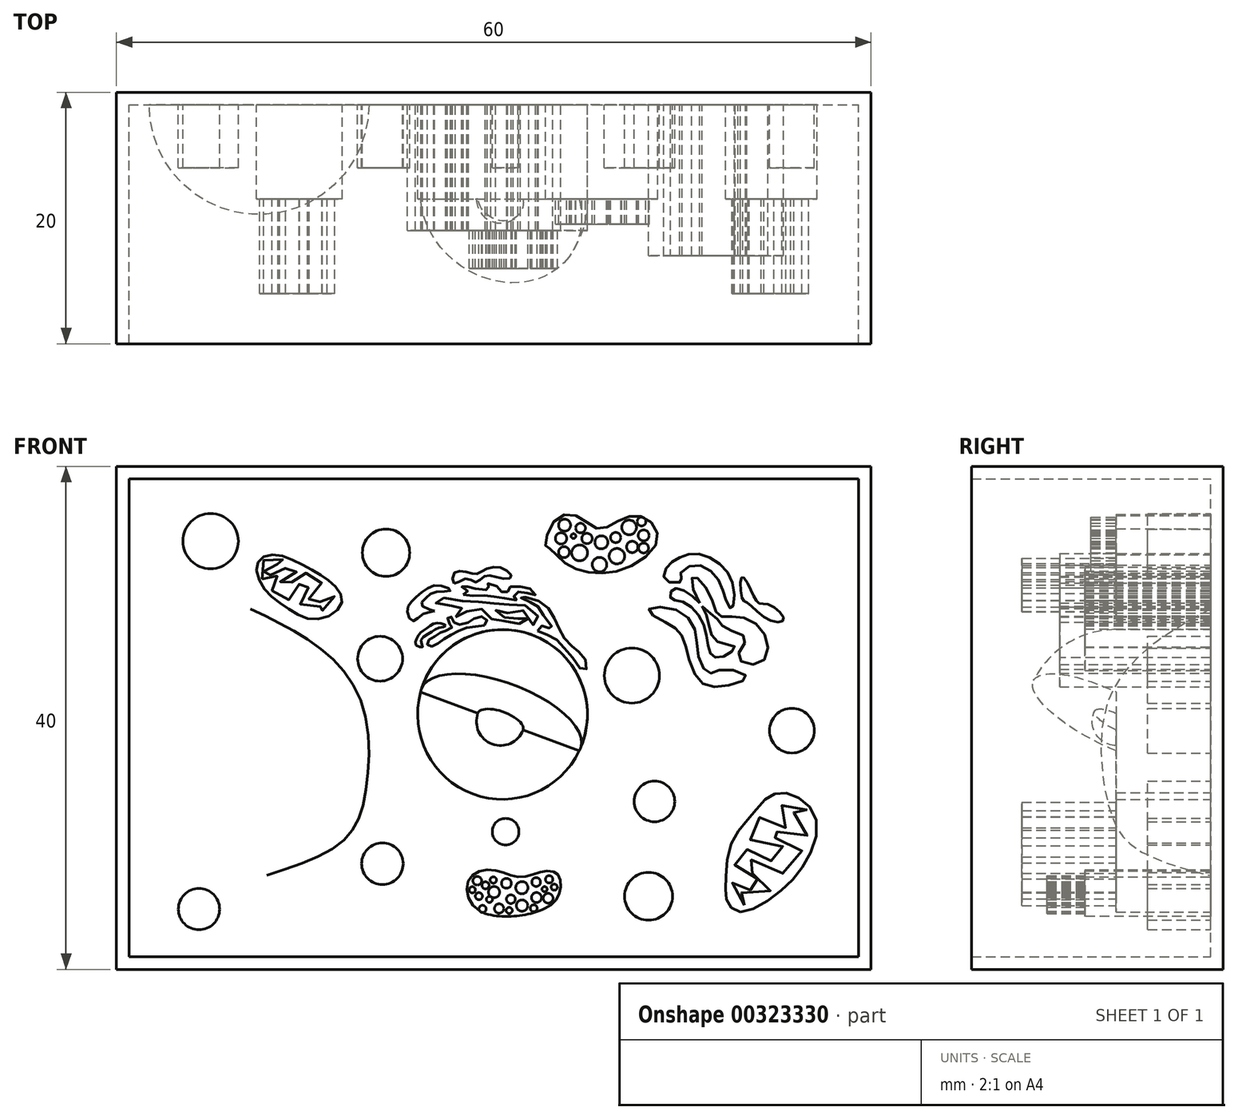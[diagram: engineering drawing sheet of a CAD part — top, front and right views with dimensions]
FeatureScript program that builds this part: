
annotation { "Feature Type Name" : "Feature", "Feature Type Description" : "" }
export const myFeature = defineFeature(function(context is Context, id is Id, definition is map)
    precondition{}
    {
        {
            var Q0;
            Q0=qCreatedBy(makeId("Front.planeOp"),FACE);
            var sketch = newSketch(context, id + "F0", { "sketchPlane" : qUnion([Q0])});
            skLineSegment(sketch, "E0.bottom", {"start": v(0, 0) * mm, "end": v(60, 0) * mm});
            skLineSegment(sketch, "E0.top", {"start": v(0, 40) * mm, "end": v(60, 40) * mm});
            skLineSegment(sketch, "E0.left", {"start": v(0, 0) * mm, "end": v(0, 40) * mm});
            skLineSegment(sketch, "E0.right", {"start": v(60, 0) * mm, "end": v(60, 40) * mm});
            skSolve(sketch);
        }
        {
            var Q0;
            Q0 = qSketchRegion(id + "F0", true);
            extrude(context, id + "F1", {"entities" : qUnion([Q0]), "depth" : 20 * mm});
        }
        {
            var Q0;
            Q0=makeQuery(id+"F1.opExtrude","CAP_FACE",FACE,{"disambiguationData":[OSD([sQuery(id+"F0.wireOp",EDGE,"E0.bottom"),sQuery(id+"F0.wireOp",EDGE,"E0.top"),sQuery(id+"F0.wireOp",EDGE,"E0.left"),sQuery(id+"F0.wireOp",EDGE,"E0.right")])],"isStart":false});
            shell(context, id + "F2", {"entities" : qUnion([Q0]), "thickness" : 1 * mm});
        }
        {
            var Q0;
            Q0=makeQuery(id+"F2.opShell","OFFSET_FACE",FACE,{"disambiguationData":[OSD([sQuery(id+"F0.wireOp",EDGE,"E0.bottom"),sQuery(id+"F0.wireOp",EDGE,"E0.top"),sQuery(id+"F0.wireOp",EDGE,"E0.left"),sQuery(id+"F0.wireOp",EDGE,"E0.right")])]});
            var sketch = newSketch(context, id + "F3", { "sketchPlane" : qUnion([Q0])});
            skCircle(sketch, "E1", {"center": v(30.7, 20.27) * mm, "radius": 6.75 * mm});
            skSolve(sketch);
        }
        {
            var Q0;
            Q0 = qSketchRegion(id + "F3", true);
            extrude(context, id + "F4", {"entities" : qUnion([Q0]), "operationType" : NewBodyOperationType.ADD, "depth" : 7.5 * mm});
        }
        {
            var Q0;
            Q0=makeQuery(id+"F4.opExtrude","CAP_FACE",FACE,{"disambiguationData":[OSD([sQuery(id+"F3.wireOp",EDGE,"E1")])],"isStart":false});
            var sketch = newSketch(context, id + "F5", { "sketchPlane" : qUnion([Q0])});
            skLineSegment(sketch, "E2", {"start": v(24.19, 22.06) * mm, "end": v(36.8, 17.38) * mm});
            skArc(sketch, "E3", {"start": v(36.8, 17.38) * mm, "mid": v(33.07, 26.67) * mm, "end": v(24.19, 22.06) * mm});
            skSolve(sketch);
        }
        {
            var Q0;
            {var subQ0=sQuery(id+"F5.wireOp",EDGE,"E2");Q0=makeQuery(id+"F5.imprint","IMPRINT",FACE,{"disambiguationData":[TD([[makeQuery(id+"F5.imprint","IMPRINT",EDGE,{"derivedFrom":subQ0}),1.0]])]});}
            var Q1;
            Q1=sQuery(id+"F5.wireOp",EDGE,"E2");
            revolve(context, id + "F6", {"operationType" : NewBodyOperationType.ADD, "entities" : qUnion([Q0]), "axis" : qUnion([Q1]), "revolveType" : RevolveType.ONE_DIRECTION, "angle" : 65 * degree});
        }
        {
            var Q0;
            Q0=makeQuery(id+"F4.opExtrude","CAP_FACE",FACE,{"disambiguationData":[OSD([sQuery(id+"F3.wireOp",EDGE,"E1")])],"isStart":false});
            var sketch = newSketch(context, id + "F7", { "sketchPlane" : qUnion([Q0])});
            skLineSegment(sketch, "E4", {"start": v(28.74, 20.37) * mm, "end": v(32.34, 19.04) * mm});
            skArc(sketch, "E5", {"start": v(28.74, 20.37) * mm, "mid": v(29.88, 17.92) * mm, "end": v(32.34, 19.04) * mm});
            skSolve(sketch);
        }
        {
            var Q0;
            Q0 = qSketchRegion(id + "F7", true);
            var Q1;
            Q1=sQuery(id+"F7.wireOp",EDGE,"E4");
            revolve(context, id + "F8", {"operationType" : NewBodyOperationType.ADD, "entities" : qUnion([Q0]), "axis" : qUnion([Q1]), "revolveType" : RevolveType.FULL});
        }
        {
            var Q0;
            Q0=makeQuery(id+"F2.opShell","OFFSET_FACE",FACE,{"disambiguationData":[OSD([sQuery(id+"F0.wireOp",EDGE,"E0.bottom"),sQuery(id+"F0.wireOp",EDGE,"E0.top"),sQuery(id+"F0.wireOp",EDGE,"E0.left"),sQuery(id+"F0.wireOp",EDGE,"E0.right")])]});
            var sketch = newSketch(context, id + "F9", { "sketchPlane" : qUnion([Q0])});
            skFitSpline(sketch, "E6", {"points": [v(25.07, 25.66) * mm, v(25.73, 26.04) * mm, v(26.42, 26.5) * mm, v(27.33, 26.99) * mm, v(28.44, 27.27) * mm, v(29.4, 27.44) * mm, v(29.35, 27.95) * mm, v(28.58, 27.98) * mm, v(27.9, 27.55) * mm, v(27, 27.46) * mm, v(26.76, 27.82) * mm, v(26.47, 28.12) * mm, v(26.35, 27.59) * mm, v(26.73, 27.3) * mm, v(26.23, 26.93) * mm, v(25.84, 26.83) * mm, v(25.25, 26.45) * mm, v(24.8, 26.14) * mm, v(24.73, 25.8) * mm, v(25.07, 25.66) * mm]});
            skFitSpline(sketch, "E7", {"points": [v(26.2, 27.32) * mm, v(25.62, 27.15) * mm, v(24.9, 26.76) * mm, v(24.22, 26.14) * mm, v(24.34, 25.63) * mm, v(23.84, 25.8) * mm, v(23.84, 26.21) * mm, v(24.15, 26.75) * mm, v(24.72, 27.15) * mm, v(25.35, 27.53) * mm, v(25.99, 27.48) * mm, v(26.2, 27.32) * mm]});
            skSolve(sketch);
        }
        {
            var Q0;
            Q0=makeQuery(id+"F9.imprint","IMPRINT",FACE,{"disambiguationData":[TD([[makeQuery(id+"F9.imprint","IMPRINT",EDGE,{"derivedFrom":sQuery(id+"F9.wireOp",EDGE,"E7")}),-1.0]])]});
            var Q1;
            Q1 = qSketchRegion(id + "F9", true);
            extrude(context, id + "F10", {"entities" : qUnion([Q0, Q1]), "operationType" : NewBodyOperationType.ADD, "depth" : 10 * mm});
        }
        {
            var Q0;
            Q0=makeQuery(id+"F2.opShell","OFFSET_FACE",FACE,{"disambiguationData":[OSD([sQuery(id+"F0.wireOp",EDGE,"E0.bottom"),sQuery(id+"F0.wireOp",EDGE,"E0.top"),sQuery(id+"F0.wireOp",EDGE,"E0.left"),sQuery(id+"F0.wireOp",EDGE,"E0.right")])]});
            var sketch = newSketch(context, id + "F11", { "sketchPlane" : qUnion([Q0])});
            skFitSpline(sketch, "E8", {"points": [v(26.99, 28.02) * mm, v(27.51, 28.27) * mm, v(28.27, 28.62) * mm, v(29.25, 28.56) * mm, v(29.78, 27.9) * mm, v(30.36, 27.74) * mm, v(31.23, 27.66) * mm, v(32.28, 27.48) * mm, v(32.78, 27.77) * mm, v(32.43, 28.08) * mm, v(31.95, 27.9) * mm, v(31.2, 27.96) * mm, v(30.45, 28.12) * mm, v(30.16, 28.55) * mm, v(30.74, 28.44) * mm, v(31.44, 28.36) * mm, v(32.56, 28.45) * mm, v(33.23, 27.33) * mm, v(33.55, 27.76) * mm, v(33.02, 28.7) * mm, v(31.85, 29.04) * mm, v(30.88, 28.99) * mm, v(29.86, 29.13) * mm, v(28.79, 29.22) * mm, v(27.74, 29.26) * mm, v(26.35, 29.56) * mm, v(25.24, 29.25) * mm, v(25.9, 29.02) * mm, v(26.92, 28.88) * mm, v(27.5, 28.76) * mm, v(27.06, 28.46) * mm, v(26.99, 28.02) * mm]});
            skFitSpline(sketch, "E9", {"points": [v(33.49, 26.9) * mm, v(34.5, 26.54) * mm, v(35.36, 25.83) * mm, v(36.4, 24.63) * mm, v(37.08, 23.77) * mm, v(37.46, 24.13) * mm, v(36.9, 25.12) * mm, v(36.34, 25.6) * mm, v(35.54, 26.42) * mm, v(35.04, 27.45) * mm, v(34.4, 28.64) * mm, v(33.2, 29.42) * mm, v(32.1, 29.62) * mm, v(32.67, 29.3) * mm, v(33.44, 28.94) * mm, v(34.02, 28.09) * mm, v(34.68, 27.1) * mm, v(34.21, 27.22) * mm, v(33.76, 27.29) * mm, v(33.49, 26.9) * mm]});
            skFitSpline(sketch, "E10", {"points": [v(27.58, 29.8) * mm, v(28.4, 29.72) * mm, v(29.4, 29.71) * mm, v(30.23, 29.6) * mm, v(31.24, 29.47) * mm, v(31.92, 29.39) * mm, v(31.55, 29.77) * mm, v(31.95, 30.04) * mm, v(32.63, 29.94) * mm, v(33.3, 29.76) * mm, v(33.09, 30.16) * mm, v(32.34, 30.39) * mm, v(31.52, 30.48) * mm, v(31.05, 30.25) * mm, v(31.1, 29.94) * mm, v(30.63, 30.03) * mm, v(30.31, 30.4) * mm, v(29.83, 30.66) * mm, v(29.32, 30.6) * mm, v(29.76, 30.25) * mm, v(29.03, 30.2) * mm, v(28.35, 30.34) * mm, v(27.9, 30.45) * mm, v(27.56, 30.52) * mm, v(27.47, 30.25) * mm, v(27.98, 30.04) * mm, v(27.58, 29.8) * mm]});
            skFitSpline(sketch, "E11", {"points": [v(25.29, 28.49) * mm, v(24.44, 28.3) * mm, v(23.58, 27.7) * mm, v(23.13, 28.46) * mm, v(23.44, 29.22) * mm, v(24.47, 30.11) * mm, v(25.72, 30.54) * mm, v(26.57, 30.13) * mm, v(25.44, 30.03) * mm, v(24.56, 29.5) * mm, v(24.27, 28.96) * mm, v(25.29, 28.49) * mm]});
            skFitSpline(sketch, "E12", {"points": [v(26.84, 30.68) * mm, v(27.83, 31.09) * mm, v(28.62, 30.8) * mm, v(29.31, 31.3) * mm, v(30.43, 31.13) * mm, v(31.4, 31.2) * mm, v(30.82, 31.84) * mm, v(29.5, 31.9) * mm, v(28.66, 31.45) * mm, v(27.85, 31.6) * mm, v(26.85, 31.52) * mm, v(26.84, 30.68) * mm]});
            skSolve(sketch);
        }
        {
            var Q0;
            Q0 = qSketchRegion(id + "F11", true);
            extrude(context, id + "F12", {"entities" : qUnion([Q0]), "operationType" : NewBodyOperationType.ADD, "depth" : 10 * mm});
        }
        {
            var Q0;
            Q0=makeQuery(id+"F2.opShell","OFFSET_FACE",FACE,{"disambiguationData":[OSD([sQuery(id+"F0.wireOp",EDGE,"E0.bottom"),sQuery(id+"F0.wireOp",EDGE,"E0.top"),sQuery(id+"F0.wireOp",EDGE,"E0.left"),sQuery(id+"F0.wireOp",EDGE,"E0.right")])]});
            var sketch = newSketch(context, id + "F13", { "sketchPlane" : qUnion([Q0])});
            skLineSegment(sketch, "E13", {"start": v(11.95, 7.47) * mm, "end": v(10.66, 28.67) * mm});
            skFitSpline(sketch, "E14", {"points": [v(11.95, 7.47) * mm, v(17.96, 10.16) * mm, v(19.78, 13.87) * mm, v(19.5, 21.18) * mm, v(15.85, 25.79) * mm, v(10.66, 28.67) * mm], "startDerivative": vector(33.09, 10.9) * mm, "endDerivative": vector(-26.92, 12.89) * mm});
            skSolve(sketch);
        }
        {
            var Q0;
            Q0 = qSketchRegion(id + "F13", true);
            var Q1;
            Q1=sQuery(id+"F13.wireOp",EDGE,"E13");
            revolve(context, id + "F14", {"operationType" : NewBodyOperationType.ADD, "entities" : qUnion([Q0]), "axis" : qUnion([Q1]), "revolveType" : RevolveType.ONE_DIRECTION, "oppositeDirection" : true, "angle" : 180 * degree});
        }
        {
            var Q0;
            Q0=makeQuery(id+"F2.opShell","OFFSET_FACE",FACE,{"disambiguationData":[OSD([sQuery(id+"F0.wireOp",EDGE,"E0.bottom"),sQuery(id+"F0.wireOp",EDGE,"E0.top"),sQuery(id+"F0.wireOp",EDGE,"E0.left"),sQuery(id+"F0.wireOp",EDGE,"E0.right")])]});
            var sketch = newSketch(context, id + "F15", { "sketchPlane" : qUnion([Q0])});
            skFitSpline(sketch, "E15", {"points": [v(49.62, 4.57) * mm, v(52.42, 5.92) * mm, v(54.71, 8.4) * mm, v(55.64, 11.92) * mm, v(53.81, 13.85) * mm, v(52.04, 13.84) * mm, v(50.53, 12.3) * mm, v(48.9, 10.02) * mm, v(48.45, 6.71) * mm, v(48.6, 5.34) * mm, v(49.62, 4.57) * mm]});
            skSolve(sketch);
        }
        {
            var Q0;
            Q0 = qSketchRegion(id + "F15", true);
            extrude(context, id + "F16", {"entities" : qUnion([Q0]), "operationType" : NewBodyOperationType.ADD, "depth" : 7.5 * mm});
        }
        {
            var Q0;
            Q0=makeQuery(id+"F16.opExtrude","CAP_FACE",FACE,{"disambiguationData":[OSD([sQuery(id+"F15.wireOp",EDGE,"E15")])],"isStart":false});
            var sketch = newSketch(context, id + "F17", { "sketchPlane" : qUnion([Q0])});
            skFitSpline(sketch, "E16", {"points": [v(49.92, 5.09) * mm, v(49.15, 5.47) * mm, v(49.05, 6.42) * mm, v(48.98, 7.17) * mm, v(49.5, 6.87) * mm, v(50.32, 6.35) * mm, v(51.27, 6.21) * mm, v(51.43, 6.81) * mm, v(50.55, 7.34) * mm, v(49.68, 7.7) * mm, v(49.18, 8.24) * mm, v(49.37, 9.3) * mm, v(49.9, 9.82) * mm, v(50.4, 9.2) * mm, v(51.19, 8.84) * mm, v(52.02, 8.66) * mm, v(52.86, 8.5) * mm, v(53.21, 9.46) * mm, v(52.5, 9.98) * mm, v(50.96, 10.23) * mm, v(50.25, 10.44) * mm, v(50.55, 11.47) * mm, v(51.12, 12.1) * mm, v(51.81, 11.77) * mm, v(52.76, 11.28) * mm, v(53.54, 11.44) * mm, v(53.4, 12.28) * mm, v(52.93, 13.06) * mm, v(53.47, 13.28) * mm, v(54.33, 13.1) * mm, v(55.03, 12.4) * mm, v(54.48, 12.2) * mm, v(53.9, 12.62) * mm, v(54.04, 12.06) * mm, v(54.94, 11.5) * mm, v(54.8, 10.51) * mm, v(53.77, 10.71) * mm, v(52.4, 10.94) * mm, v(51.26, 11.05) * mm, v(52.25, 10.5) * mm, v(53.76, 10.1) * mm, v(54.51, 9.58) * mm, v(54.07, 8.6) * mm, v(53.4, 7.72) * mm, v(52.1, 7.77) * mm, v(50.88, 8.38) * mm, v(50, 8.91) * mm, v(49.89, 8) * mm, v(51.12, 7.57) * mm, v(52.28, 7.01) * mm, v(51.72, 5.97) * mm, v(50.64, 5.65) * mm, v(49.65, 6.07) * mm, v(49.8, 5.52) * mm, v(50.32, 5.1) * mm, v(49.92, 5.09) * mm]});
            skSolve(sketch);
        }
        {
            var Q0;
            Q0 = qSketchRegion(id + "F17", true);
            extrude(context, id + "F18", {"entities" : qUnion([Q0]), "operationType" : NewBodyOperationType.ADD, "depth" : 7.5 * mm});
        }
        {
            var Q0;
            Q0=makeQuery(id+"F2.opShell","OFFSET_FACE",FACE,{"disambiguationData":[OSD([sQuery(id+"F0.wireOp",EDGE,"E0.bottom"),sQuery(id+"F0.wireOp",EDGE,"E0.top"),sQuery(id+"F0.wireOp",EDGE,"E0.left"),sQuery(id+"F0.wireOp",EDGE,"E0.right")])]});
            var sketch = newSketch(context, id + "F19", { "sketchPlane" : qUnion([Q0])});
            skFitSpline(sketch, "E17", {"points": [v(11.25, 32.39) * mm, v(11.62, 30.45) * mm, v(13.62, 28.7) * mm, v(15.98, 27.84) * mm, v(17.92, 29.13) * mm, v(17.2, 30.66) * mm, v(15.32, 31.89) * mm, v(12.75, 32.96) * mm, v(11.25, 32.39) * mm]});
            skSolve(sketch);
        }
        {
            var Q0;
            Q0 = qSketchRegion(id + "F19", true);
            extrude(context, id + "F20", {"entities" : qUnion([Q0]), "operationType" : NewBodyOperationType.ADD, "depth" : 7.5 * mm});
        }
        {
            var Q0;
            Q0=makeQuery(id+"F20.opExtrude","CAP_FACE",FACE,{"disambiguationData":[OSD([sQuery(id+"F19.wireOp",EDGE,"E17")])],"isStart":false});
            var sketch = newSketch(context, id + "F21", { "sketchPlane" : qUnion([Q0])});
            skFitSpline(sketch, "E18", {"points": [v(11.57, 31.04) * mm, v(11.4, 32) * mm, v(11.89, 32.64) * mm, v(12.63, 32.63) * mm, v(13.44, 32.5) * mm, v(13.26, 32.15) * mm, v(12.69, 32.25) * mm, v(12, 32.17) * mm, v(11.74, 31.49) * mm, v(12.19, 30.86) * mm, v(12.3, 31.55) * mm, v(12.97, 31.8) * mm, v(13.7, 31.94) * mm, v(14.52, 31.82) * mm, v(13.92, 31.43) * mm, v(13.22, 31.18) * mm, v(13.03, 30.4) * mm, v(13.63, 30.58) * mm, v(14.4, 31.25) * mm, v(14.91, 31.55) * mm, v(15.68, 31.22) * mm, v(16.3, 30.77) * mm, v(16.12, 30.06) * mm, v(15.2, 29.28) * mm, v(15.75, 28.83) * mm, v(16.56, 29.76) * mm, v(17.19, 29.83) * mm, v(17.27, 29.16) * mm, v(16.39, 28.5) * mm, v(16.77, 29.34) * mm, v(15.7, 28.5) * mm, v(14.72, 28.87) * mm, v(14.6, 29.6) * mm, v(15.26, 30.37) * mm, v(15.22, 30.98) * mm, v(14.5, 30.6) * mm, v(13.8, 29.85) * mm, v(13.63, 29.32) * mm, v(12.55, 29.84) * mm, v(12.46, 30.53) * mm, v(12.85, 31.38) * mm, v(12.07, 30.6) * mm, v(11.57, 31.04) * mm]});
            skSolve(sketch);
        }
        {
            var Q0;
            Q0 = qSketchRegion(id + "F21", true);
            extrude(context, id + "F22", {"entities" : qUnion([Q0]), "operationType" : NewBodyOperationType.ADD, "depth" : 7.5 * mm});
        }
        {
            var Q0;
            Q0=makeQuery(id+"F2.opShell","OFFSET_FACE",FACE,{"disambiguationData":[OSD([sQuery(id+"F0.wireOp",EDGE,"E0.bottom"),sQuery(id+"F0.wireOp",EDGE,"E0.top"),sQuery(id+"F0.wireOp",EDGE,"E0.left"),sQuery(id+"F0.wireOp",EDGE,"E0.right")])]});
            var sketch = newSketch(context, id + "F23", { "sketchPlane" : qUnion([Q0])});
            skFitSpline(sketch, "E19", {"points": [v(43.64, 27.6) * mm, v(44.81, 26.79) * mm, v(45.42, 25.03) * mm, v(46.5, 22.8) * mm, v(48.48, 22.56) * mm, v(50.1, 23.25) * mm, v(48.26, 23.86) * mm, v(47.14, 23.57) * mm, v(46.32, 24.75) * mm, v(45.96, 27.12) * mm, v(44.21, 28.69) * mm, v(42.3, 28.58) * mm, v(43.64, 27.6) * mm]});
            skFitSpline(sketch, "E20", {"points": [v(47.16, 25.29) * mm, v(46.67, 27.5) * mm, v(45.03, 29.22) * mm, v(44.06, 29.53) * mm, v(44.28, 30.25) * mm, v(45.72, 29.75) * mm, v(46.94, 28.1) * mm, v(47.71, 26.12) * mm, v(49.17, 25.62) * mm, v(47.93, 24.79) * mm, v(47.16, 25.29) * mm]});
            skFitSpline(sketch, "E21", {"points": [v(48.44, 27.14) * mm, v(50.03, 26.29) * mm, v(49.44, 24.82) * mm, v(51.24, 24.4) * mm, v(51.59, 26.55) * mm, v(49.47, 28.06) * mm, v(47.92, 28.12) * mm, v(47.2, 29.8) * mm, v(45.83, 31.23) * mm, v(46.38, 29.13) * mm, v(47.65, 27.97) * mm, v(48.44, 27.14) * mm]});
            skFitSpline(sketch, "E22", {"points": [v(48.47, 29.36) * mm, v(47.75, 31.16) * mm, v(45.9, 32.15) * mm, v(44.8, 31.29) * mm, v(44.97, 30.87) * mm, v(43.69, 30.9) * mm, v(43.74, 31.91) * mm, v(44.65, 32.68) * mm, v(46.13, 33.06) * mm, v(48.08, 32.15) * mm, v(49.1, 30.26) * mm, v(48.9, 28.7) * mm, v(48.47, 29.36) * mm]});
            skFitSpline(sketch, "E23", {"points": [v(50.14, 29.16) * mm, v(51.97, 27.75) * mm, v(53.06, 27.85) * mm, v(51.9, 29) * mm, v(51.06, 29.14) * mm, v(50.43, 30.23) * mm, v(49.74, 31.19) * mm, v(49.77, 29.46) * mm, v(50.14, 29.16) * mm]});
            skSolve(sketch);
        }
        {
            var Q0;
            Q0 = qSketchRegion(id + "F23", true);
            extrude(context, id + "F24", {"entities" : qUnion([Q0]), "operationType" : NewBodyOperationType.ADD, "depth" : 12 * mm});
        }
        {
            var Q0;
            Q0=makeQuery(id+"F2.opShell","OFFSET_FACE",FACE,{"disambiguationData":[OSD([sQuery(id+"F0.wireOp",EDGE,"E0.bottom"),sQuery(id+"F0.wireOp",EDGE,"E0.top"),sQuery(id+"F0.wireOp",EDGE,"E0.left"),sQuery(id+"F0.wireOp",EDGE,"E0.right")])]});
            var sketch = newSketch(context, id + "F25", { "sketchPlane" : qUnion([Q0])});
            skFitSpline(sketch, "E24", {"points": [v(34.05, 4.84) * mm, v(31.2, 4.22) * mm, v(28.37, 5.05) * mm, v(28.08, 7.24) * mm, v(30.02, 7.89) * mm, v(32.06, 7.35) * mm, v(34.01, 7.8) * mm, v(35.13, 7.52) * mm, v(35.2, 6) * mm, v(34.05, 4.84) * mm]});
            skSolve(sketch);
        }
        {
            var Q0;
            Q0 = qSketchRegion(id + "F25", true);
            extrude(context, id + "F26", {"entities" : qUnion([Q0]), "operationType" : NewBodyOperationType.ADD, "depth" : 10 * mm});
        }
        {
            var Q0;
            Q0=makeQuery(id+"F26.opExtrude","CAP_FACE",FACE,{"disambiguationData":[OSD([sQuery(id+"F25.wireOp",EDGE,"E24")])],"isStart":false});
            var sketch = newSketch(context, id + "F27", { "sketchPlane" : qUnion([Q0])});
            skCircle(sketch, "E25", {"center": v(28.3, 6.33) * mm, "radius": 0.25 * mm});
            skCircle(sketch, "E26", {"center": v(29.35, 6.68) * mm, "radius": 0.28 * mm});
            skCircle(sketch, "E27", {"center": v(28.7, 7.05) * mm, "radius": 0.35 * mm});
            skCircle(sketch, "E28", {"center": v(28.82, 5.82) * mm, "radius": 0.28 * mm});
            skCircle(sketch, "E29", {"center": v(29.11, 4.8) * mm, "radius": 0.29 * mm});
            skCircle(sketch, "E30", {"center": v(29.66, 5.56) * mm, "radius": 0.24 * mm});
            skCircle(sketch, "E31", {"center": v(30.03, 6.15) * mm, "radius": 0.45 * mm});
            skCircle(sketch, "E32", {"center": v(29.97, 7.1) * mm, "radius": 0.25 * mm});
            skCircle(sketch, "E33", {"center": v(31, 6.84) * mm, "radius": 0.4 * mm});
            skCircle(sketch, "E34", {"center": v(30.43, 4.84) * mm, "radius": 0.37 * mm});
            skCircle(sketch, "E35", {"center": v(31.36, 5.58) * mm, "radius": 0.35 * mm});
            skCircle(sketch, "E36", {"center": v(32.24, 6.5) * mm, "radius": 0.49 * mm});
            skCircle(sketch, "E37", {"center": v(33.37, 6.95) * mm, "radius": 0.35 * mm});
            skCircle(sketch, "E38", {"center": v(32.26, 5.08) * mm, "radius": 0.45 * mm});
            skCircle(sketch, "E39", {"center": v(33.4, 5.71) * mm, "radius": 0.4 * mm});
            skCircle(sketch, "E40", {"center": v(34.04, 6.38) * mm, "radius": 0.2 * mm});
            skCircle(sketch, "E41", {"center": v(34.4, 7.16) * mm, "radius": 0.3 * mm});
            skCircle(sketch, "E42", {"center": v(34.33, 5.66) * mm, "radius": 0.39 * mm});
            skCircle(sketch, "E43", {"center": v(34.81, 6.54) * mm, "radius": 0.24 * mm});
            skCircle(sketch, "E44", {"center": v(33.18, 4.86) * mm, "radius": 0.28 * mm});
            skCircle(sketch, "E45", {"center": v(31.23, 4.68) * mm, "radius": 0.24 * mm});
            skSolve(sketch);
        }
        {
            var Q0;
            Q0 = qSketchRegion(id + "F27", true);
            extrude(context, id + "F28", {"entities" : qUnion([Q0]), "operationType" : NewBodyOperationType.ADD, "depth" : 3 * mm});
        }
        {
            var Q0;
            Q0=makeQuery(id+"F2.opShell","OFFSET_FACE",FACE,{"disambiguationData":[OSD([sQuery(id+"F0.wireOp",EDGE,"E0.bottom"),sQuery(id+"F0.wireOp",EDGE,"E0.top"),sQuery(id+"F0.wireOp",EDGE,"E0.left"),sQuery(id+"F0.wireOp",EDGE,"E0.right")])]});
            var sketch = newSketch(context, id + "F29", { "sketchPlane" : qUnion([Q0])});
            skFitSpline(sketch, "E46", {"points": [v(34.46, 33.46) * mm, v(35.6, 32.37) * mm, v(37.7, 31.55) * mm, v(40.58, 31.93) * mm, v(43.02, 34.14) * mm, v(42.14, 35.84) * mm, v(40.25, 35.86) * mm, v(38.43, 35.04) * mm, v(36.73, 36) * mm, v(34.9, 35.76) * mm, v(34.14, 33.66) * mm, v(34.46, 33.46) * mm]});
            skSolve(sketch);
        }
        {
            var Q0;
            Q0=makeQuery(id+"F29.imprint","IMPRINT",FACE,{"disambiguationData":[TD([[makeQuery(id+"F29.imprint","IMPRINT",EDGE,{"derivedFrom":sQuery(id+"F29.wireOp",EDGE,"E46")}),1.0]])]});
            extrude(context, id + "F30", {"entities" : qUnion([Q0]), "operationType" : NewBodyOperationType.ADD, "depth" : 7.5 * mm});
        }
        {
            var Q0;
            Q0=makeQuery(id+"F30.opExtrude","CAP_FACE",FACE,{"disambiguationData":[OSD([sQuery(id+"F29.wireOp",EDGE,"E46")])],"isStart":false});
            var sketch = newSketch(context, id + "F31", { "sketchPlane" : qUnion([Q0])});
            skCircle(sketch, "E47", {"center": v(35.35, 34.27) * mm, "radius": 0.45 * mm});
            skCircle(sketch, "E48", {"center": v(36.9, 35.1) * mm, "radius": 0.39 * mm});
            skCircle(sketch, "E49", {"center": v(36.83, 33.13) * mm, "radius": 0.63 * mm});
            skCircle(sketch, "E50", {"center": v(38.56, 33.96) * mm, "radius": 0.52 * mm});
            skCircle(sketch, "E51", {"center": v(38.41, 32.19) * mm, "radius": 0.58 * mm});
            skCircle(sketch, "E52", {"center": v(37.41, 34.26) * mm, "radius": 0.42 * mm});
            skCircle(sketch, "E53", {"center": v(35.63, 35.32) * mm, "radius": 0.48 * mm});
            skCircle(sketch, "E54", {"center": v(39.8, 32.86) * mm, "radius": 0.62 * mm});
            skCircle(sketch, "E55", {"center": v(39.7, 34.34) * mm, "radius": 0.4 * mm});
            skCircle(sketch, "E56", {"center": v(40.77, 35.15) * mm, "radius": 0.58 * mm});
            skCircle(sketch, "E57", {"center": v(41.02, 33.6) * mm, "radius": 0.45 * mm});
            skCircle(sketch, "E58", {"center": v(41.93, 34.5) * mm, "radius": 0.44 * mm});
            skCircle(sketch, "E59", {"center": v(41.92, 33.5) * mm, "radius": 0.4 * mm});
            skCircle(sketch, "E60", {"center": v(41.76, 35.62) * mm, "radius": 0.35 * mm});
            skCircle(sketch, "E61", {"center": v(35.6, 33.18) * mm, "radius": 0.44 * mm});
            skCircle(sketch, "E62", {"center": v(36.34, 34.46) * mm, "radius": 0.19 * mm});
            skSolve(sketch);
        }
        {
            var Q0;
            Q0 = qSketchRegion(id + "F31", true);
            extrude(context, id + "F32", {"entities" : qUnion([Q0]), "operationType" : NewBodyOperationType.ADD, "depth" : 2 * mm});
        }
        {
            var Q0;
            Q0=makeQuery(id+"F2.opShell","OFFSET_FACE",FACE,{"disambiguationData":[OSD([sQuery(id+"F0.wireOp",EDGE,"E0.bottom"),sQuery(id+"F0.wireOp",EDGE,"E0.top"),sQuery(id+"F0.wireOp",EDGE,"E0.left"),sQuery(id+"F0.wireOp",EDGE,"E0.right")])]});
            var sketch = newSketch(context, id + "F33", { "sketchPlane" : qUnion([Q0])});
            skCircle(sketch, "E63", {"center": v(21.15, 8.4) * mm, "radius": 1.65 * mm});
            skCircle(sketch, "E64", {"center": v(42.78, 13.36) * mm, "radius": 1.61 * mm});
            skCircle(sketch, "E65", {"center": v(42.3, 5.81) * mm, "radius": 1.9 * mm});
            skCircle(sketch, "E66", {"center": v(7.49, 34.05) * mm, "radius": 2.2 * mm});
            skCircle(sketch, "E67", {"center": v(21.44, 33.14) * mm, "radius": 1.88 * mm});
            skCircle(sketch, "E68", {"center": v(53.71, 18.99) * mm, "radius": 1.78 * mm});
            skCircle(sketch, "E69", {"center": v(40.99, 23.37) * mm, "radius": 2.2 * mm});
            skCircle(sketch, "E70", {"center": v(30.95, 10.95) * mm, "radius": 1.06 * mm});
            skCircle(sketch, "E71", {"center": v(20.96, 24.7) * mm, "radius": 1.79 * mm});
            skCircle(sketch, "E72", {"center": v(6.56, 4.79) * mm, "radius": 1.64 * mm});
            skSolve(sketch);
        }
        {
            var Q0;
            Q0 = qSketchRegion(id + "F33", true);
            extrude(context, id + "F34", {"entities" : qUnion([Q0]), "operationType" : NewBodyOperationType.ADD, "depth" : 5 * mm});
        }
    });
